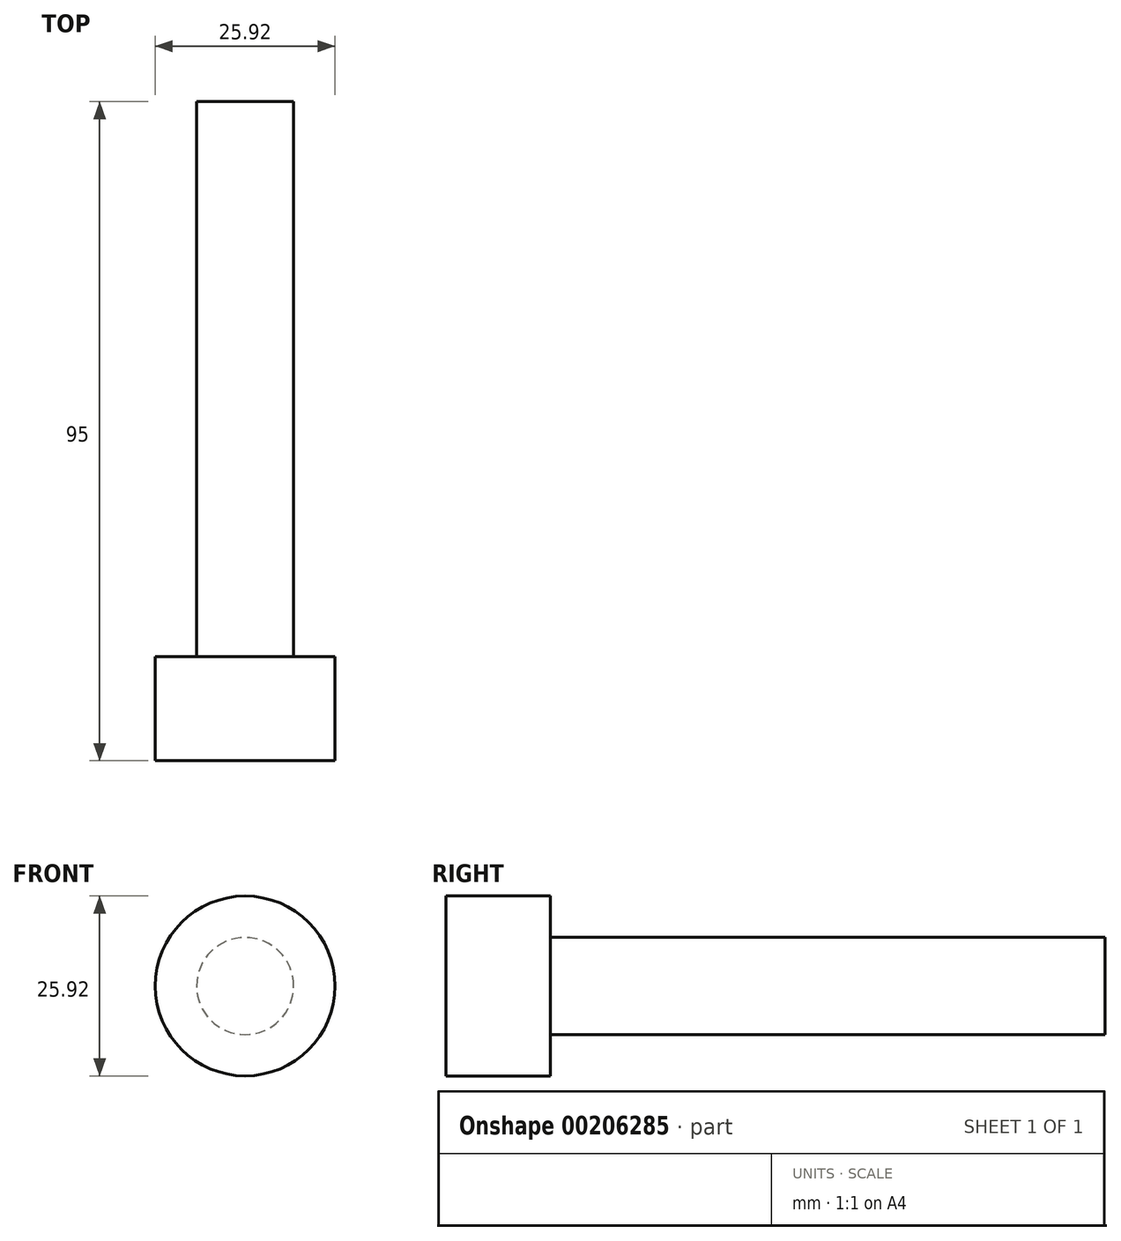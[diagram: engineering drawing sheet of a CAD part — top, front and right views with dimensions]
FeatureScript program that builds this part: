
annotation { "Feature Type Name" : "Feature", "Feature Type Description" : "" }
export const myFeature = defineFeature(function(context is Context, id is Id, definition is map)
    precondition{}
    {
        {
            var Q0;
            Q0=qCreatedBy(makeId("Front.planeOp"),FACE);
            var sketch = newSketch(context, id + "F0", { "sketchPlane" : qUnion([Q0])});
            skCircle(sketch, "E0", {"center": v(0, 0) * mm, "radius": 7 * mm});
            skSolve(sketch);
        }
        {
            var Q0;
            Q0=makeQuery(id+"F0.imprint","IMPRINT",FACE,{"disambiguationData":[TD([[makeQuery(id+"F0.imprint","IMPRINT",EDGE,{"derivedFrom":sQuery(id+"F0.wireOp",EDGE,"E0")}),1.0]])]});
            extrude(context, id + "F1", {"entities" : qUnion([Q0]), "depth" : 80 * mm});
        }
        {
            var Q0;
            Q0=makeQuery(id+"F1.opExtrude","CAP_FACE",FACE,{"disambiguationData":[OSD([sQuery(id+"F0.wireOp",EDGE,"E0")])],"isStart":false});
            var sketch = newSketch(context, id + "F2", { "sketchPlane" : qUnion([Q0])});
            skCircle(sketch, "E1", {"center": v(0, 0) * mm, "radius": 12.96 * mm});
            skSolve(sketch);
        }
        {
            var Q0;
            Q0=makeQuery(id+"F2.imprint","IMPRINT",FACE,{"disambiguationData":[TD([[makeQuery(id+"F2.imprint","IMPRINT",EDGE,{"derivedFrom":sQuery(id+"F2.wireOp",EDGE,"E1")}),1.0]])]});
            var Q1;
            Q1=makeQuery(id+"F2.imprint","IMPRINT",FACE,{"disambiguationData":[TD([[makeQuery(id+"F2.imprint","IMPRINT",EDGE,{"derivedFrom":makeQuery(id+"F1.opExtrude","CAP_EDGE",EDGE,{"disambiguationData":[OSD([sQuery(id+"F0.wireOp",EDGE,"E0")])],"isStart":false})}),1.0]])]});
            extrude(context, id + "F3", {"entities" : qUnion([Q0, Q1]), "depth" : 15 * mm});
        }
    });
